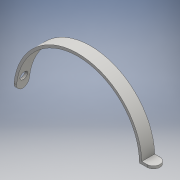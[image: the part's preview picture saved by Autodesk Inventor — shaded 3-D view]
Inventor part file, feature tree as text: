
AUTODESK INVENTOR PART (.ipt)
format: ipt  version: 2016 (Build 200138000, 138)  size: 151,552 bytes
history: native  units: mm
features: extrude x4, sketch x4, plane x1
ambient origin geometry x8: Origin, YZ Plane, XZ Plane, XY Plane, X Axis, Y Axis, Z Axis, Center Point
bodies: Solid1 (feature_tree)
feature tree (9):
  extrude  "Extrusion1"  Depth=5.0mm TaperAngle=0.0deg
  extrude  "Extrusion2"  Depth=3.0mm TaperAngle=0.0deg
  plane  "Work Plane1"
  extrude  "Extrusion3"  Depth=3.0mm
  extrude  "Extrusion4"  [1 undecoded]
  sketch  "Sketch1"  dims[d4=5.0mm d5=0.0mm d7=5.0mm d8=0.0mm]
  sketch  "Sketch2"  dims[d9=-25.0mm d13=3.0mm d14=0.0mm]
  sketch  "Sketch3"  dims[d15=4.5mm d16=3.0mm]
  sketch  "Sketch4"  dims[d17=4.0mm d18=0.0mm]
note: 1 required parameter value undecoded (feature->parameter linkage not recoverable at this tier; creation-order binding heuristic only, values carry confidence <= 0.55)
